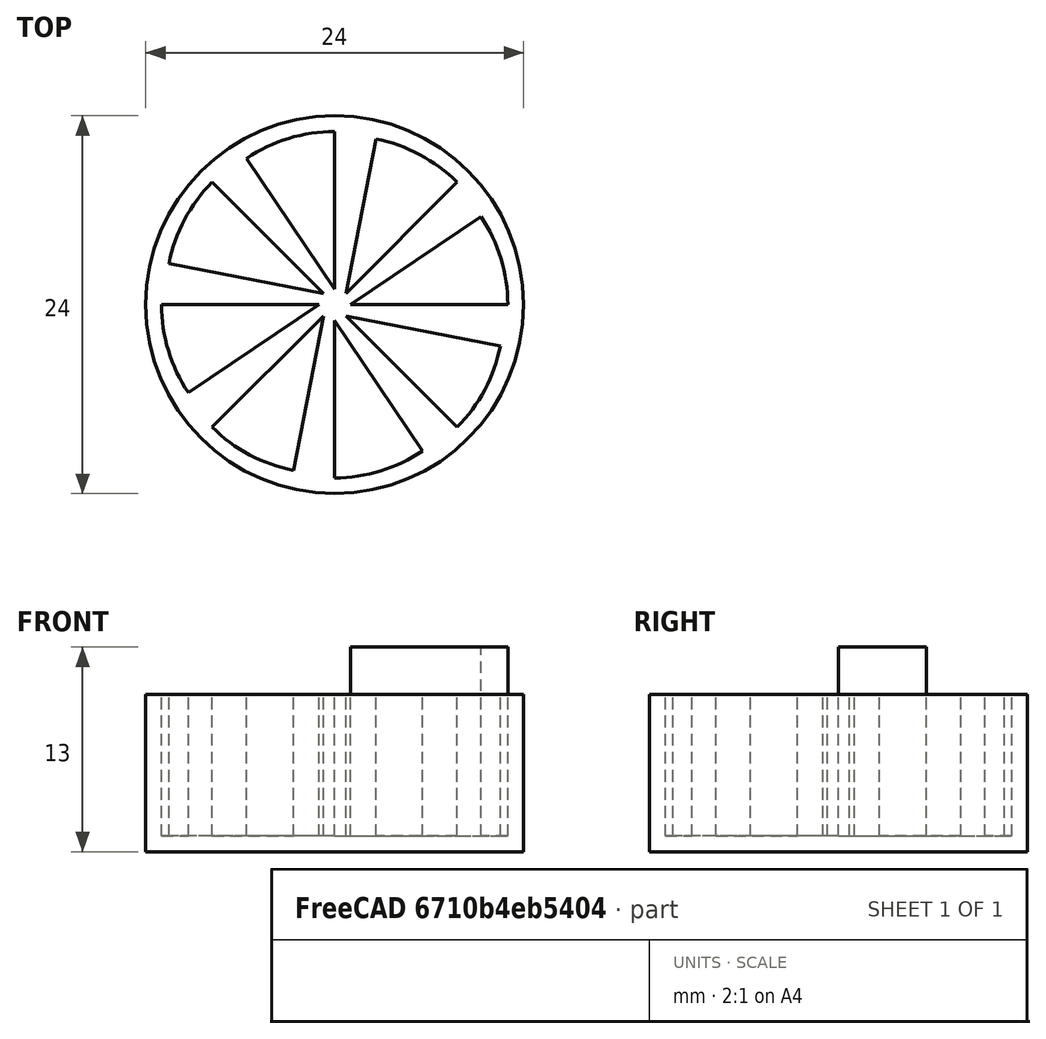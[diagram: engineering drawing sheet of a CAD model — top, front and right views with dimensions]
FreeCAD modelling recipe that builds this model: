
FCSTD DOCUMENT  (FreeCAD 0.21R33694 (Git))
Label: OJT1_T11R02_trivial
License: All rights reserved
LicenseURL: http://en.wikipedia.org/wiki/All_rights_reserved
objects: Part::Cylinder×3, Part::FeaturePython×1, Part::Cut×1
note: 4 computed .brp shape members not serialized (recipe doc carries the construction recipe); baked Part::Feature solids carry a one-line shape summary decoded from their .brp

FEATURE [Part::Cylinder] Cylinder
  Angle = 360
  AttacherType = Attacher::AttachEngine3D
  FirstAngle = 0
  Height = 10
  Radius = 12
  SecondAngle = 0
FEATURE [Part::Cylinder] Cylinder001
  Angle = 34
  AttacherType = Attacher::AttachEngine3D
  FirstAngle = 0
  Height = 12
  Placement = pos=(1,0,1) rot=(0,0,1;0rad)
  Radius = 10
  SecondAngle = 0
FEATURE [Part::FeaturePython] Array  # Draft array (typed FeaturePython)
  AlwaysSyncPlacement = false
  Angle = 360
  ArrayType = 1
  Axis = (0,0,1)
  Base = -> Cylinder001
  Center = (0,0,0)
  Count = 8
  ExpandArray = false
  Fuse = false
  IntervalAxis = (0,0,0)
  IntervalX = (50,0,0)
  IntervalY = (0,50,0)
  IntervalZ = (0,0,50)
  NumberCircles = 3
  NumberPolar = 8
  NumberX = 2
  NumberY = 2
  NumberZ = 1
  PlacementList = 8 placements: [(1,0,1),(0.707107,0.707107,1),(0,1,1),(-0.707107,0.707107,1),(-1,1.22465e-16,1),(-0.707107,-0.707107,1),(-2.22045e-16,-1,1),(0.707107,-0.707107,1)]
  RadialDistance = 50
  ScaleList = (8) [(1,1,1),(1,1,1),(1,1,1),(1,1,1),(1,1,1),(1,1,1),(1,1,1),(1,1,1)]
  Symmetry = 1
  TangentialDistance = 25
FEATURE [Part::Cut] Cut
  Base = -> Cylinder
  Refine = true
  Tool = -> Array
FEATURE [Part::Cylinder] Cylinder002
  Angle = 34
  AttacherType = Attacher::AttachEngine3D
  FirstAngle = 0
  Height = 12
  Placement = pos=(1,0,1) rot=(0,0,1;0rad)
  Radius = 10
  SecondAngle = 0
